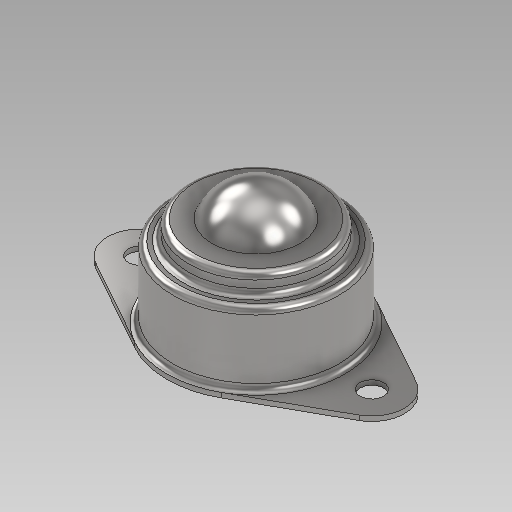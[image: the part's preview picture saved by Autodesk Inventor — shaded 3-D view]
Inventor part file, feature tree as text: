
AUTODESK INVENTOR PART (.ipt)
format: ipt  version: 2020 (Build 240168000, 168)  size: 286,208 bytes
history: native  units: mm
features: sketch x4, revolve x2, extrude x2
ambient origin geometry x8: Origin, YZ Plane, XZ Plane, XY Plane, X Axis, Y Axis, Z Axis, Center Point
bodies: Solid1 (feature_tree)
feature tree (8):
  revolve  "Revolution1"  [1 undecoded]
  extrude  "Extrusion1"  Depth=0.8mm
  extrude  "Extrusion2"  Depth=13.0625mm
  revolve  "Revolution2"  [1 undecoded]
  sketch  "Sketch1"  dims[d0=14.0mm d1=15.875mm]
  sketch  "Sketch2"  dims[d2=25.0mm d3=0.8mm]
  sketch  "Sketch3"  dims[d4=16.0mm d5=13.0625mm]
  sketch  "Sketch5"  dims[d6=1.0mm d8=1.4mm d9=1.0mm d10=0.5mm d11=90.0deg d12=39.0mm d13=4.0mm d14=4.0mm d15=19.5mm d16=10.0mm d17=0.0mm d18=15.2mm d19=0.0mm d20=13.063mm d21=15.875mm d22=90.0deg]
note: 2 required parameter values undecoded (feature->parameter linkage not recoverable at this tier; creation-order binding heuristic only, values carry confidence <= 0.55)
